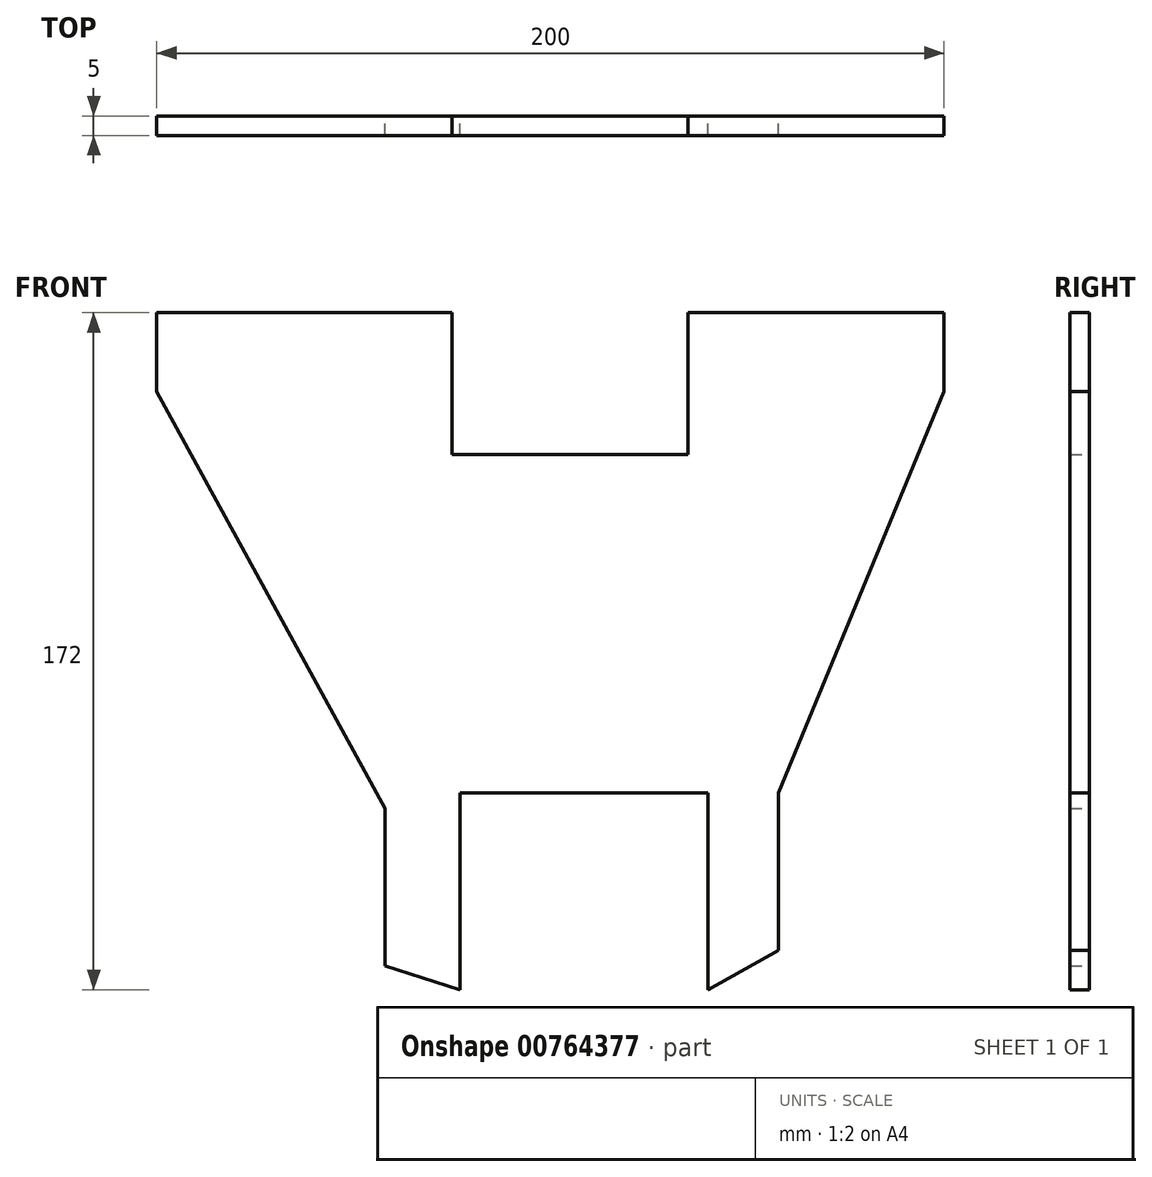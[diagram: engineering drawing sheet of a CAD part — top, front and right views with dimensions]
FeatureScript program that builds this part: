
annotation { "Feature Type Name" : "Feature", "Feature Type Description" : "" }
export const myFeature = defineFeature(function(context is Context, id is Id, definition is map)
    precondition{}
    {
        {
            var Q0;
            Q0=qCreatedBy(makeId("Front.planeOp"),FACE);
            var sketch = newSketch(context, id + "F0", { "sketchPlane" : qUnion([Q0])});
            skLineSegment(sketch, "E0", {"start": v(92, 122) * mm, "end": v(92, 102) * mm});
            skLineSegment(sketch, "E1", {"start": v(50, 0) * mm, "end": v(92, 102) * mm});
            skLineSegment(sketch, "E2", {"start": v(92, 122) * mm, "end": v(27, 122) * mm});
            skLineSegment(sketch, "E3", {"start": v(-33, 122) * mm, "end": v(-33, 86) * mm});
            skLineSegment(sketch, "E4", {"start": v(27, 122) * mm, "end": v(27, 86) * mm});
            skLineSegment(sketch, "E5", {"start": v(27, 86) * mm, "end": v(-33, 86) * mm});
            skLineSegment(sketch, "E6", {"start": v(-33, 122) * mm, "end": v(-108, 122) * mm});
            skLineSegment(sketch, "E7", {"start": v(-108, 122) * mm, "end": v(-108, 102) * mm});
            skLineSegment(sketch, "E8", {"start": v(-108, 102) * mm, "end": v(-50, -4) * mm});
            skLineSegment(sketch, "E9", {"start": v(0, 0) * mm, "end": v(32, 0) * mm});
            skLineSegment(sketch, "E10", {"start": v(32, 0) * mm, "end": v(32, -50) * mm});
            skLineSegment(sketch, "E11", {"start": v(50, 0) * mm, "end": v(50, -40) * mm});
            skLineSegment(sketch, "E12", {"start": v(32, -50) * mm, "end": v(50, -40) * mm});
            skLineSegment(sketch, "E13", {"start": v(0, 0) * mm, "end": v(-31, 0) * mm});
            skLineSegment(sketch, "E14", {"start": v(-31, 0) * mm, "end": v(-31, -50) * mm});
            skLineSegment(sketch, "E15", {"start": v(-50, -4) * mm, "end": v(-50, -44) * mm});
            skLineSegment(sketch, "E16", {"start": v(-50, -44) * mm, "end": v(-31, -50) * mm});
            skSolve(sketch);
        }
        {
            var Q0;
            Q0=makeQuery(id+"F0.imprint","IMPRINT",FACE,{"disambiguationData":[TD([[makeQuery(id+"F0.imprint","IMPRINT",EDGE,{"derivedFrom":sQuery(id+"F0.wireOp",EDGE,"s2blPv4o-Mztw-SOad-0KaV-Lwdq33GFjQxP")}),1.0]])]});
            var Q1;
            Q1=makeQuery(id+"F0.imprint","IMPRINT",FACE,{"disambiguationData":[TD([[makeQuery(id+"F0.imprint","IMPRINT",EDGE,{"derivedFrom":sQuery(id+"F0.wireOp",EDGE,"E0")}),-1.0]])]});
            extrude(context, id + "F1", {"entities" : qUnion([Q0, Q1]), "depth" : 5 * mm, "offsetDistance" : 25 * mm, "symmetric" : true});
        }
    });
